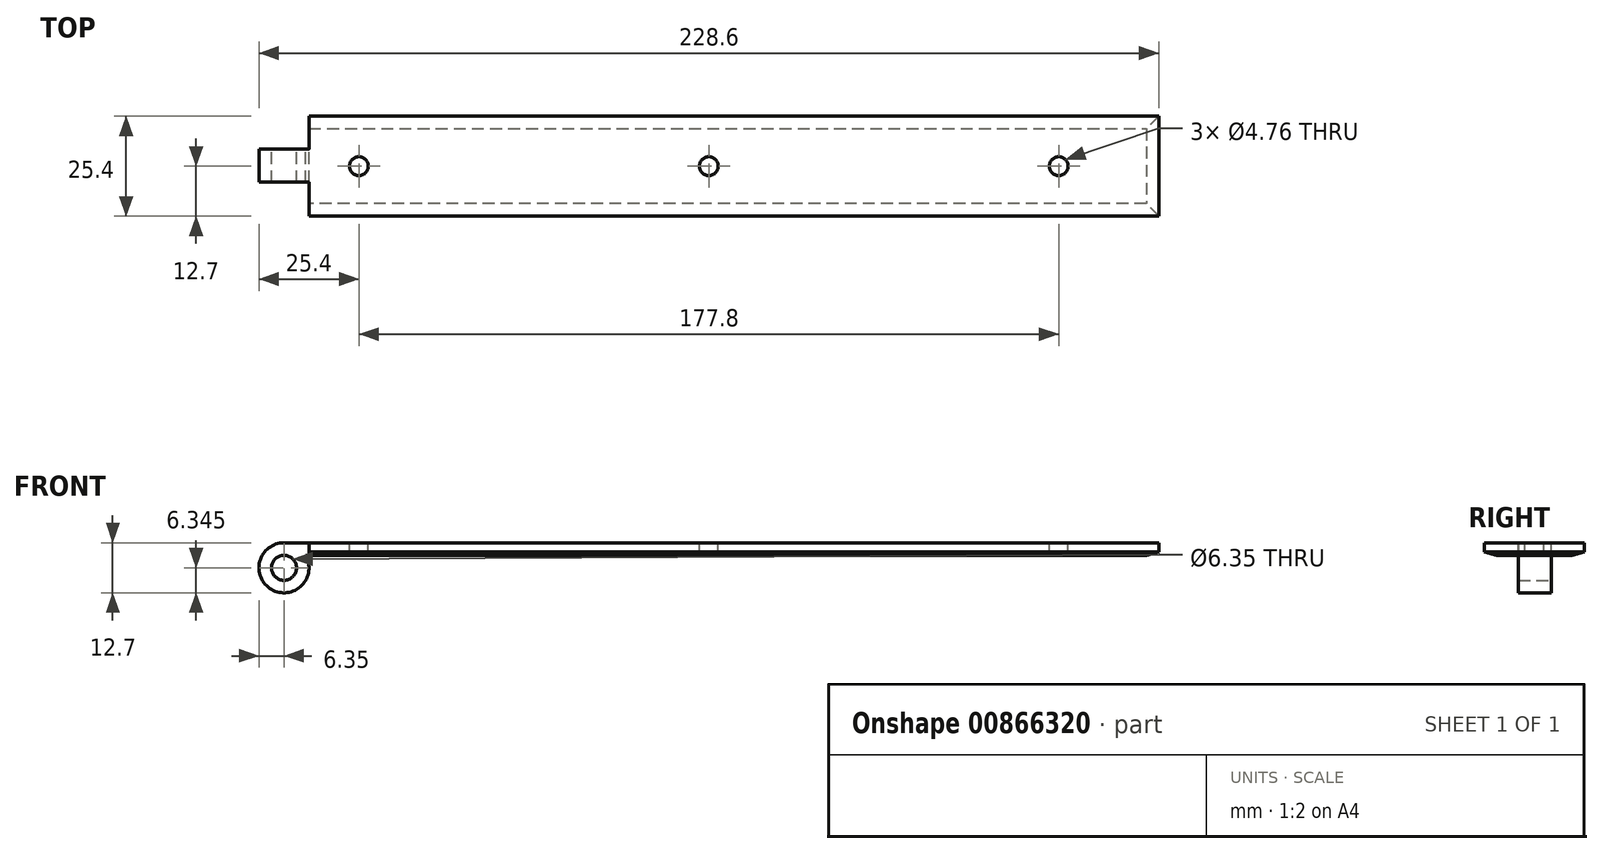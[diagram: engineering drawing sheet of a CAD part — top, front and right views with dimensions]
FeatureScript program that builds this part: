
annotation { "Feature Type Name" : "Feature", "Feature Type Description" : "" }
export const myFeature = defineFeature(function(context is Context, id is Id, definition is map)
    precondition{}
    {
        {
            var Q0;
            Q0=qCreatedBy(makeId("Front.planeOp"),FACE);
            var sketch = newSketch(context, id + "F0", { "sketchPlane" : qUnion([Q0])});
            skLineSegment(sketch, "E0.bottom", {"start": v(11.85, 0) * mm, "end": v(228.6, 0) * mm});
            skLineSegment(sketch, "E0.top", {"start": v(6.35, 3.18) * mm, "end": v(228.6, 3.18) * mm});
            skLineSegment(sketch, "E0.right", {"start": v(228.6, 0) * mm, "end": v(228.6, 3.18) * mm});
            skCircle(sketch, "E1", {"center": v(6.35, -3.18) * mm, "radius": 3.18 * mm});
            skArc(sketch, "E2.0", {"start": v(6.35, 3.18) * mm, "mid": v(3.18, -8.67) * mm, "end": v(11.85, 0) * mm});
            skSolve(sketch);
        }
        {
            var Q0;
            Q0=makeQuery(id+"F0.imprint","IMPRINT",FACE,{"disambiguationData":[TD([[makeQuery(id+"F0.imprint","IMPRINT",EDGE,{"derivedFrom":sQuery(id+"F0.wireOp",EDGE,"E0.bottom")}),1.0]])]});
            extrude(context, id + "F1", {"entities" : qUnion([Q0]), "depth" : 25.4 * mm, "offsetDistance" : 25.4 * mm});
        }
        {
            var Q0;
            Q0=makeQuery(id+"F1.opExtrude","SWEPT_FACE",FACE,{"disambiguationData":[OSD([sQuery(id+"F0.wireOp",EDGE,"E0.top")])]});
            var sketch = newSketch(context, id + "F2", { "sketchPlane" : qUnion([Q0])});
            skCircle(sketch, "E3", {"center": v(203.2, -12.7) * mm, "radius": 2.38 * mm});
            skPoint(sketch, "E3.centerSnap0", {"position": v(228.6, -12.7) * mm});
            skCircle(sketch, "E4.1.0.0", {"center": v(114.3, -12.7) * mm, "radius": 2.38 * mm});
            skCircle(sketch, "E4.2.0.0", {"center": v(25.4, -12.7) * mm, "radius": 2.38 * mm});
            skLineSegment(sketch, "E4.direction1", {"start": v(203.2, -12.7) * mm, "end": v(114.3, -12.7) * mm, "construction": true});
            skLineSegment(sketch, "E5", {"start": v(12.7, 5.42) * mm, "end": v(12.7, -8.38) * mm});
            skLineSegment(sketch, "E6", {"start": v(12.7, -8.38) * mm, "end": v(0, -8.38) * mm});
            skLineSegment(sketch, "E7", {"start": v(0, -8.38) * mm, "end": v(0, -16.76) * mm});
            skLineSegment(sketch, "E8", {"start": v(0, -16.76) * mm, "end": v(12.7, -16.76) * mm});
            skLineSegment(sketch, "E9", {"start": v(12.7, -16.76) * mm, "end": v(12.7, -32.81) * mm});
            skLineSegment(sketch, "E10", {"start": v(12.7, -32.81) * mm, "end": v(-5.86, -32.81) * mm});
            skLineSegment(sketch, "E11", {"start": v(-5.86, -32.81) * mm, "end": v(-5.86, 5.42) * mm});
            skLineSegment(sketch, "E12", {"start": v(-5.86, 5.42) * mm, "end": v(12.7, 5.42) * mm});
            skSolve(sketch);
        }
        {
            var Q0;
            Q0 = qSketchRegion(id + "F2", true);
            extrude(context, id + "F3", {"entities" : qUnion([Q0]), "operationType" : NewBodyOperationType.REMOVE, "endBound" : BoundingType.THROUGH_ALL, "oppositeDirection" : true, "depth" : 25.4 * mm, "offsetDistance" : 25.4 * mm});
        }
        {
            var Q0;
            Q0=makeQuery(id+"F1.opExtrude","CAP_EDGE",EDGE,{"disambiguationData":[OSD([sQuery(id+"F0.wireOp",EDGE,"E0.bottom")])],"isStart":false});
            var Q1;
            Q1=makeQuery(id+"F1.opExtrude","CAP_EDGE",EDGE,{"disambiguationData":[OSD([sQuery(id+"F0.wireOp",EDGE,"E0.bottom")])],"isStart":true});
            var Q2;
            Q2=makeQuery(id+"F1.opExtrude","SWEPT_EDGE",EDGE,{"disambiguationData":[OSD([sQuery(id+"F0.wireOp",EDGE,"E0.bottom"),sQuery(id+"F0.wireOp",EDGE,"E0.right")])]});
            chamfer(context, id + "F4", {"entities" : qUnion([Q0, Q1, Q2]), "chamferType" : ChamferType.TWO_OFFSETS, "width1" : 0.8 * mm, "oppositeDirection" : false, "width2" : 3.17 * mm, "tangentPropagation" : true});
        }
    });
